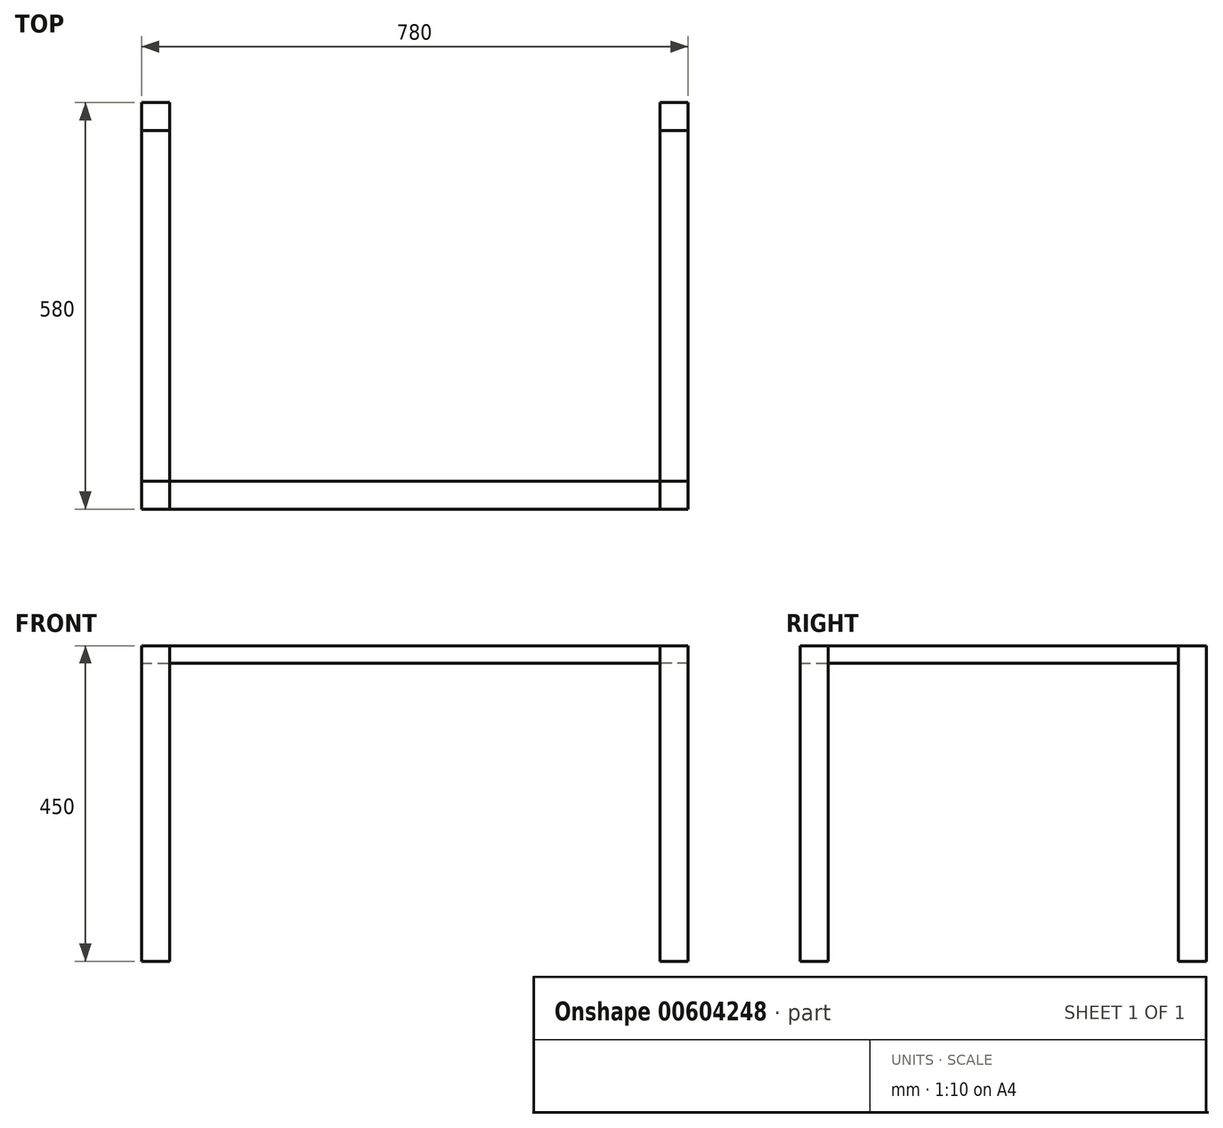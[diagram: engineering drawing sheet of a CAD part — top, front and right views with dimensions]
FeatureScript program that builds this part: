
annotation { "Feature Type Name" : "Feature", "Feature Type Description" : "" }
export const myFeature = defineFeature(function(context is Context, id is Id, definition is map)
    precondition{}
    {
        {
            var Q0;
            Q0=qCreatedBy(makeId("Top.planeOp"),FACE);
            cPlane(context, id + "F0", {"entities" : qUnion([Q0]), "cplaneType" : CPlaneType.OFFSET, "offset" : 600 * mm, "width" : 150 * mm, "height" : 150 * mm});
        }
        {
            var Q0;
            Q0=qCreatedBy(id+"F0.planeOp",FACE);
            var sketch = newSketch(context, id + "F1", { "sketchPlane" : qUnion([Q0])});
            skLineSegment(sketch, "E0", {"start": v(-63.03, 83.64) * mm, "end": v(636.97, 83.64) * mm});
            skLineSegment(sketch, "E1.bottom", {"start": v(-63.03, 83.64) * mm, "end": v(-103.03, 83.64) * mm, "construction": true});
            skLineSegment(sketch, "E1.top", {"start": v(-63.03, 43.64) * mm, "end": v(-103.03, 43.64) * mm, "construction": true});
            skLineSegment(sketch, "E1.left", {"start": v(-63.03, 83.64) * mm, "end": v(-63.03, 43.64) * mm, "construction": true});
            skLineSegment(sketch, "E1.right", {"start": v(-103.03, 83.64) * mm, "end": v(-103.03, 43.64) * mm, "construction": true});
            skLineSegment(sketch, "E2", {"start": v(-63.03, 43.64) * mm, "end": v(-63.03, -456.36) * mm, "construction": true});
            skLineSegment(sketch, "E3.bottom", {"start": v(-63.03, -456.36) * mm, "end": v(-103.03, -456.36) * mm, "construction": true});
            skLineSegment(sketch, "E3.top", {"start": v(-63.03, -496.36) * mm, "end": v(-103.03, -496.36) * mm, "construction": true});
            skLineSegment(sketch, "E3.left", {"start": v(-63.03, -456.36) * mm, "end": v(-63.03, -496.36) * mm, "construction": true});
            skLineSegment(sketch, "E3.right", {"start": v(-103.03, -456.36) * mm, "end": v(-103.03, -496.36) * mm, "construction": true});
            skLineSegment(sketch, "E4", {"start": v(-103.03, 43.64) * mm, "end": v(-103.03, -456.36) * mm, "construction": true});
            skLineSegment(sketch, "E5", {"start": v(-63.03, -456.36) * mm, "end": v(636.97, -456.36) * mm, "construction": true});
            skLineSegment(sketch, "E6", {"start": v(636.97, -456.36) * mm, "end": v(636.97, 43.64) * mm, "construction": true});
            skLineSegment(sketch, "E7.bottom", {"start": v(636.97, 83.64) * mm, "end": v(676.97, 83.64) * mm, "construction": true});
            skLineSegment(sketch, "E7.top", {"start": v(636.97, 43.64) * mm, "end": v(676.97, 43.64) * mm, "construction": true});
            skLineSegment(sketch, "E7.left", {"start": v(636.97, 83.64) * mm, "end": v(636.97, 43.64) * mm, "construction": true});
            skLineSegment(sketch, "E7.right", {"start": v(676.97, 83.64) * mm, "end": v(676.97, 43.64) * mm, "construction": true});
            skLineSegment(sketch, "E8.bottom", {"start": v(636.97, -456.36) * mm, "end": v(676.97, -456.36) * mm, "construction": true});
            skLineSegment(sketch, "E8.top", {"start": v(636.97, -496.36) * mm, "end": v(676.97, -496.36) * mm, "construction": true});
            skLineSegment(sketch, "E8.left", {"start": v(636.97, -456.36) * mm, "end": v(636.97, -496.36) * mm, "construction": true});
            skLineSegment(sketch, "E8.right", {"start": v(676.97, -456.36) * mm, "end": v(676.97, -496.36) * mm, "construction": true});
            skLineSegment(sketch, "E9", {"start": v(676.97, 43.64) * mm, "end": v(676.97, -456.36) * mm, "construction": true});
            skLineSegment(sketch, "E10", {"start": v(-63.03, -496.36) * mm, "end": v(636.97, -496.36) * mm, "construction": true});
            skLineSegment(sketch, "E11", {"start": v(636.97, 43.64) * mm, "end": v(-63.03, 43.64) * mm, "construction": true});
            skLineSegment(sketch, "E12.bottom", {"start": v(-63.03, 43.64) * mm, "end": v(636.97, 43.64) * mm});
            skLineSegment(sketch, "E12.top", {"start": v(-63.03, -456.36) * mm, "end": v(636.97, -456.36) * mm});
            skLineSegment(sketch, "E12.left", {"start": v(-63.03, 43.64) * mm, "end": v(-63.03, -456.36) * mm});
            skLineSegment(sketch, "E12.right", {"start": v(636.97, 43.64) * mm, "end": v(636.97, -456.36) * mm});
            skLineSegment(sketch, "E13.left", {"start": v(-63.03, 83.64) * mm, "end": v(-63.03, 43.64) * mm});
            skLineSegment(sketch, "E13.right", {"start": v(636.97, 83.64) * mm, "end": v(636.97, 43.64) * mm});
            skLineSegment(sketch, "E14.bottom", {"start": v(676.97, 43.64) * mm, "end": v(636.97, 43.64) * mm});
            skLineSegment(sketch, "E14.top", {"start": v(676.97, -456.36) * mm, "end": v(636.97, -456.36) * mm});
            skLineSegment(sketch, "E14.left", {"start": v(676.97, 43.64) * mm, "end": v(676.97, -456.36) * mm});
            skLineSegment(sketch, "E15.bottom", {"start": v(636.97, -496.36) * mm, "end": v(-63.03, -496.36) * mm});
            skLineSegment(sketch, "E15.top", {"start": v(636.97, -456.36) * mm, "end": v(-63.03, -456.36) * mm});
            skLineSegment(sketch, "E15.left", {"start": v(636.97, -496.36) * mm, "end": v(636.97, -456.36) * mm});
            skLineSegment(sketch, "E15.right", {"start": v(-63.03, -496.36) * mm, "end": v(-63.03, -456.36) * mm});
            skLineSegment(sketch, "E16.bottom", {"start": v(-103.03, -456.36) * mm, "end": v(-63.03, -456.36) * mm});
            skLineSegment(sketch, "E16.top", {"start": v(-103.03, 43.64) * mm, "end": v(-63.03, 43.64) * mm});
            skLineSegment(sketch, "E16.left", {"start": v(-103.03, -456.36) * mm, "end": v(-103.03, 43.64) * mm});
            skLineSegment(sketch, "E16.right", {"start": v(-63.03, -456.36) * mm, "end": v(-63.03, 43.64) * mm});
            skLineSegment(sketch, "E17.bottom", {"start": v(-103.03, 83.64) * mm, "end": v(-63.03, 83.64) * mm});
            skLineSegment(sketch, "E17.left", {"start": v(-103.03, 83.64) * mm, "end": v(-103.03, 43.64) * mm});
            skLineSegment(sketch, "E18.bottom", {"start": v(676.97, 83.64) * mm, "end": v(636.97, 83.64) * mm});
            skLineSegment(sketch, "E18.left", {"start": v(676.97, 83.64) * mm, "end": v(676.97, 43.64) * mm});
            skLineSegment(sketch, "E19.bottom", {"start": v(676.97, -496.36) * mm, "end": v(636.97, -496.36) * mm});
            skLineSegment(sketch, "E19.left", {"start": v(676.97, -496.36) * mm, "end": v(676.97, -456.36) * mm});
            skLineSegment(sketch, "E20.bottom", {"start": v(-103.03, -496.36) * mm, "end": v(-63.03, -496.36) * mm});
            skLineSegment(sketch, "E20.left", {"start": v(-103.03, -496.36) * mm, "end": v(-103.03, -456.36) * mm});
            skSolve(sketch);
        }
        {
            var Q0;
            Q0=makeQuery(id+"F1.imprint","IMPRINT",FACE,{"disambiguationData":[TD([[makeQuery(id+"F1.imprint","IMPRINT",EDGE,{"derivedFrom":sQuery(id+"F1.wireOp",EDGE,"E20.bottom")}),1.0]])]});
            var Q1;
            Q1=makeQuery(id+"F1.imprint","IMPRINT",FACE,{"disambiguationData":[TD([[makeQuery(id+"F1.imprint","IMPRINT",EDGE,{"derivedFrom":sQuery(id+"F1.wireOp",EDGE,"E17.bottom")}),-1.0]])]});
            var Q2;
            Q2=makeQuery(id+"F1.imprint","IMPRINT",FACE,{"disambiguationData":[TD([[makeQuery(id+"F1.imprint","IMPRINT",EDGE,{"derivedFrom":sQuery(id+"F1.wireOp",EDGE,"E18.bottom")}),1.0]])]});
            var Q3;
            Q3=makeQuery(id+"F1.imprint","IMPRINT",FACE,{"disambiguationData":[TD([[makeQuery(id+"F1.imprint","IMPRINT",EDGE,{"derivedFrom":sQuery(id+"F1.wireOp",EDGE,"E19.bottom")}),-1.0]])]});
            extrude(context, id + "F2", {"entities" : qUnion([Q0, Q1, Q2, Q3]), "oppositeDirection" : true, "depth" : 450 * mm, "offsetDistance" : 25 * mm});
        }
        {
            var Q0;
            Q0=makeQuery(id+"F1.imprint","IMPRINT",FACE,{"disambiguationData":[TD([[makeQuery(id+"F1.imprint","IMPRINT",EDGE,{"derivedFrom":sQuery(id+"F1.wireOp",EDGE,"E15.bottom")}),-1.0]])]});
            var Q1;
            Q1=makeQuery(id+"F1.imprint","IMPRINT",FACE,{"disambiguationData":[TD([[makeQuery(id+"F1.imprint","IMPRINT",EDGE,{"derivedFrom":sQuery(id+"F1.wireOp",EDGE,"E16.left")}),-1.0]])]});
            var Q2;
            Q2=makeQuery(id+"F1.imprint","IMPRINT",FACE,{"disambiguationData":[TD([[makeQuery(id+"F1.imprint","IMPRINT",EDGE,{"derivedFrom":sQuery(id+"F1.wireOp",EDGE,"E12.bottom")}),-1.0]])]});
            var Q3;
            Q3=makeQuery(id+"F1.imprint","IMPRINT",FACE,{"disambiguationData":[TD([[makeQuery(id+"F1.imprint","IMPRINT",EDGE,{"derivedFrom":sQuery(id+"F1.wireOp",EDGE,"E14.left")}),-1.0]])]});
            var Q4;
            Q4=makeQuery(id+"F1.imprint","IMPRINT",FACE,{"disambiguationData":[TD([[makeQuery(id+"F1.imprint","IMPRINT",EDGE,{"derivedFrom":sQuery(id+"F1.wireOp",EDGE,"E0")}),-1.0]])]});
            extrude(context, id + "F3", {"entities" : qUnion([Q0, Q1, Q2, Q3, Q4]), "oppositeDirection" : true, "depth" : 25 * mm, "offsetDistance" : 25 * mm});
        }
    });
